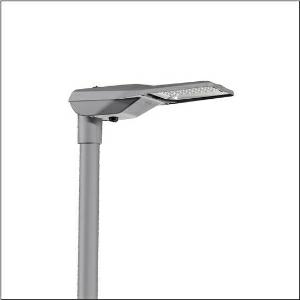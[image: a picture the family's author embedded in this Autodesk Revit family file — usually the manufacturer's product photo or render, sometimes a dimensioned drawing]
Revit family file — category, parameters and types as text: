
# Revit family: streetlight_sl_21_mini___stw1_0a_5xe2e43t08hb_75ae
name_source: partatom
category: Lighting Fixtures
units: mm (PartAtom-declared; Revit-internal decimal feet)

## family parameters
Cut with Voids When Loaded = No
Host = Face
Light Source = No
Part Type = Normal
Room Calculation Point = No
Round Connector Dimension = Use Diameter
Shared = No

## types (1)
- --- (1 x LED, 9430 lm, 66 W, 4000K)
    Apparent Load = 66 VA
    CIE Flux Codes = 38 75 98 100 100
    Color Rendering = 70
    Color Temperature = 4000K
    Default Elevation = 1800 mm
    Description = Streetlight SL 21 mini, mast luminaire, primary light control with lens, of PMMA, primary optical cover: cover, of toughened safety glass, transparent, light distribution: STW1.0a, light emission: direct distribution, primary light characteristic: asymmetric, installation type: side-entry, post-top, LED, High Power LED, rated luminous flux: 9.430lm, luminous efficacy: 143lm/W, light colour: 740, colour temperature: 4000K, control gear: D4i, control: overheat protection, constant luminous flux control, time-dependent luminous flux control, flexible luminous flux parameterisation, pre-setting: logarithmic dimming characteristic, mains connection: 220..240V, AC, 50/60Hz, start of lifetime: 66W, end of service life: 69W, reduction: 30W, luminaire housing, of diecast aluminium, powder-coated, Siteco® metallic grey (DB 702S), corrosivity category C5 mid according to DIN EN ISO 12944, please order mast flange separately, inclination adjustable: 0°, 5°, 10°, 15°, sealing non-destructively replaceable, multi-level sealing system, length: 628mm, width: 235mm, height: 110mm, mast flange for spigot size: 42mm (side-entry): 5XC10008XM4, 60/48mm (side-entry/post-top): 5XC10108XM2, 76/60mm (side-entry/post-top): 5XC10108XM1, mounting height: 4..8m, Smart Interface below and above, protection rating (complete): IP66, insulation class (complete): insulation class II (safety insulation), certification: CE, ENEC, ENEC+, VDE, impact resistance: IK10, permissible operating ambient temperature for outdoor applications: -40..+50°C, standard-compliant lighting for roads and squares, packaging unit: 1 piece

Light Distribution: STW1.0a
    Height = 110 mm
    Lamp = 1 x LED
    Lamp Light Flux = 9430 lm
    Lamp Power = 66 W
    Lamp count = 1
    Length = 625 mm
    Luminous efficacy = 143 lm/W
    Manufacturer = Siteco
    ModVariant = No
    Model = 5XE2E43T08HB
    Number of Poles = 1
    OnlyDefault = Yes
    Power Factor = 1
    Product Name = Streetlight SL 21 mini | STW1.0a
    Product group = mast luminaire | pylon top
    ProductGroupID = 6100
    Protection Class = Protection class II
    Protection Degree = IP 66
    RLX_Detail_Level = 1
    RLX_Emergency_Light_Flux = 0 lm
    RLX_Emergency_Type = 0
    RLX_Emergency_Type_DB = No
    RlxData = <blob elided: 26333 chars, md5=0fc7fc2b>
    Socket = socket
    Standby Power = 0 W
    System Light Flux = 9430 lm
    System Power = 66 W
    Type Comments = factory setting: luminous flux: 100 % | dim-lin: 254 | 670 mA
    Type Image = l_1003514.jpg
    URL = http://relux.com
    VarID = @adj_208451
    Voltage = 0 V
    Weight = 0.00 kg
    Width = 234 mm

## geometry (parser evidence)
native form markers: Blend x4, Sweep x12
no freeform markers — native parametric forms only
